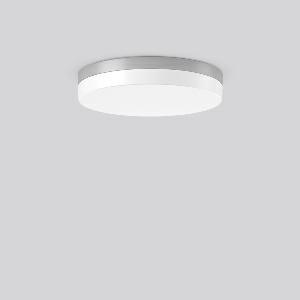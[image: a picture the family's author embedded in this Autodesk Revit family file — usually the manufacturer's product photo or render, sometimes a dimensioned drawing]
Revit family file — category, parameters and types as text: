
# Revit family: flat_slim_round_312632_004_19_6a13
name_source: partatom
category: Lighting Fixtures
units: mm (PartAtom-declared; Revit-internal decimal feet)

## family parameters
Cut with Voids When Loaded = No
Host = Face
Light Source = No
Part Type = Normal
Room Calculation Point = No
Round Connector Dimension = Use Diameter
Shared = No

## types (1)
- MultiLumen 1 830 (1 x LED Modul 830, 2400 lm, 3000)
    Apparent Load = 20 VA
    CIE Flux Codes = 39 70 90 83 100
    Color Rendering = 80
    Color Temperature = 3000
    Default Elevation = 1800 mm
    Height = 70 mm
    Lamp = 1 x LED Modul 830
    Lamp Light Flux = 2400 lm
    Lamp count = 1
    Length = 400 mm
    Lifetime = 50000 h
    Luminous efficacy = 120 lm/W
    Manufacturer = RZB
    ModVariant = No
    Model = 312632.004.19
    Mounting Place = Ceiling
    Mounting Type = Surface mounted
    Number of Poles = 1
    OnlyDefault = Yes
    Power Factor = 1
    Product Name = FLAT SLIM round
    Product group = Surface mounted ceiling and wall luminaires
    ProductGroupID = 305
    Protection Class = Protection class I
    Protection Degree = Degree of protection
    RLX_Detail_Level = 1
    RLX_Emergency_Light_Flux = 0 lm
    RLX_Emergency_Type = 0
    RLX_Emergency_Type_DB = No
    RlxData = <blob elided: 21017 chars, md5=fedf6bac>
    Socket = socket
    Standby Power = 0 W
    System Light Flux = 2400 lm
    System Power = 20 W
    Type Comments = MultiLumen 1 830
    Type Image = 312631.004.jpg
    URL = http://relux.com
    VarID = multilumen_1_830
    Voltage = 0 V
    Weight = 0.00 kg
    Width = 0 mm  [stored 0 ft]

note: [stored X ft] marks values corroborated as IEEE doubles in the binary element streams (Revit-internal decimal feet)

## geometry (parser evidence)
native form markers: Blend x4, Sweep x15
no freeform markers — native parametric forms only
